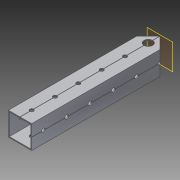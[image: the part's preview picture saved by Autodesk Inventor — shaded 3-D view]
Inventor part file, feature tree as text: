
AUTODESK INVENTOR PART (.ipt)
format: ipt  version: 2014 SP1 (Build 180222100, 222)  size: 1,223,680 bytes
history: native  units: in
note: dims shown in document units (in); Inventor stores cm internally (conversion verified against a paired STEP export)
features: extrude x3, sketch x2, pattern_circular x1, other x1, plane x1, imported_body x1
ambient origin geometry x8: Origin, YZ Plane, XZ Plane, XY Plane, X Axis, Y Axis, Z Axis, Center Point
bodies: Body1 (feature_tree)
feature tree (9):
  pattern_circular  "CirPattern2"
  other  "217-3426-STEP1"
  plane  "Work Plane1"
  extrude  "Extrusion1"  Depth=393.7008in TaperAngle=0.0deg
  extrude  "Extrusion3"  Depth=1.0in TaperAngle=0.0deg
  extrude  "Extrusion4"  TaperAngle=45.0deg  [1 undecoded]
  imported_body  "Base1"
  sketch  "Sketch1"  dims[d0=-6.0in d1=393.7008in d2=0.0in]
  sketch  "Sketch4"  dims[d8=0.5in d9=1.0in d10=0.0in d12=45.0deg d15=1.0in d16=0.375in d17=39.3701in d18=0.0in]
note: 1 required parameter value undecoded (feature->parameter linkage not recoverable at this tier; creation-order binding heuristic only, values carry confidence <= 0.55)
